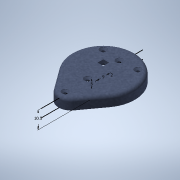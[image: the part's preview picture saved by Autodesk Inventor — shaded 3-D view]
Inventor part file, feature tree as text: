
AUTODESK INVENTOR PART (.ipt)
format: ipt  version: 2020 (Build 240168000, 168)  size: 1,116,160 bytes
history: native  units: mm
features: other x7, sketch x7, extrude x6, plane x3, boolean_combine x3, fillet x2, shell x1, hole x1, split x1, sweep x1, chamfer x1
ambient origin geometry x8: Origin, YZ Plane, XZ Plane, XY Plane, X Axis, Y Axis, Z Axis, Center Point
bodies: Body1 (feature_tree), Body2 (feature_tree), Body3 (feature_tree)
feature tree (33):
  other  "temp case"
  other  "Blocks"
  sketch  "Sketch1"  dims[d2=25.0mm d3=25.0mm]
  extrude  "Extrusion1"  Depth=25.0mm
  extrude  "Extrusion2"  Depth=2.0mm
  fillet  "Fillet2"  Radius=35.355339mm
  shell  "Shell2"  Thickness=2.0mm
  plane  "Work Plane2"
  extrude  "Extrusion6"  Depth=2.0mm TaperAngle=0.0deg
  extrude  "Extrusion7"  Depth=3.5mm
  plane  "Work Plane3"
  hole  "Hole2"  [1 undecoded]
  sketch  "Sketch4"  dims[d21=2.0mm d24=3.5mm]
  other  "Plano de corte"
  split  "Split2"
  plane  "Work Plane5"
  sweep  "Sweep1"
  boolean_combine  "Combine3"
  chamfer  "Chamfer1"  Distance=2.5mm
  extrude  "Extrusion13"  Depth=1.0mm
  boolean_combine  "Combine4"
  boolean_combine  "Combine5"
  fillet  "Fillet5"  Radius=1.5mm
  extrude  "Extrusion15"  Depth=1.0mm TaperAngle=0.0deg
  other  "tapa case"
  sketch  "Sketch2"  dims[d9=2.0mm d10=2.0mm d11=35.355339mm d12=2.0mm]
  sketch  "Sketch3"  dims[d16=12.0mm d17=0.0mm d19=2.0mm d20=0.0mm]
  sketch  "Sketch5"  dims[d25=3.5mm d28=5.0mm]
  sketch  "Sketch6"  dims[d29=5.0mm d30=5.0mm]
  other  "path"
  sketch  "Sketch10"  dims[d36=2.5mm d37=2.5mm d51=4.0mm d52=1.5mm d54=-2.0mm d57=9.0mm d58=0.0mm d68=4.0mm d69=4.0mm d70=4.0mm d71=0.117mm d72=0.0mm d73=-0.117mm d74=1.567mm d75=5.0mm d76=4.0mm d77=2.0mm d78=15.419984mm d79=5.0mm d80=0.0mm d93=4.0mm d94=4.0mm d108=0.0mm d109=0.0mm d110=4.0mm d111=2.0mm d112=45.0deg d128=23.4mm d133=1.95mm d134=1.95mm d135=19.32mm d136=2.0mm d137=30.0mm d138=2.5mm d139=2.5mm d142=6.0mm d143=3.5mm d145=5.0mm d146=10.5mm d147=5.0mm d163=0.35mm d164=180.0deg d165=0.35mm d166=90.0deg d167=5.5mm d168=0.7mm d169=1.5mm d170=0.2mm d171=19.178mm d172=0.0mm d175=2.0mm d176=0.2mm d177=0.0mm d182=2.0mm d183=9.0mm d184=1.0mm d173=0.5mm d174=0.872665mm]
  other  "back"
  other  "front"
note: 1 required parameter value undecoded (feature->parameter linkage not recoverable at this tier; creation-order binding heuristic only, values carry confidence <= 0.55)
